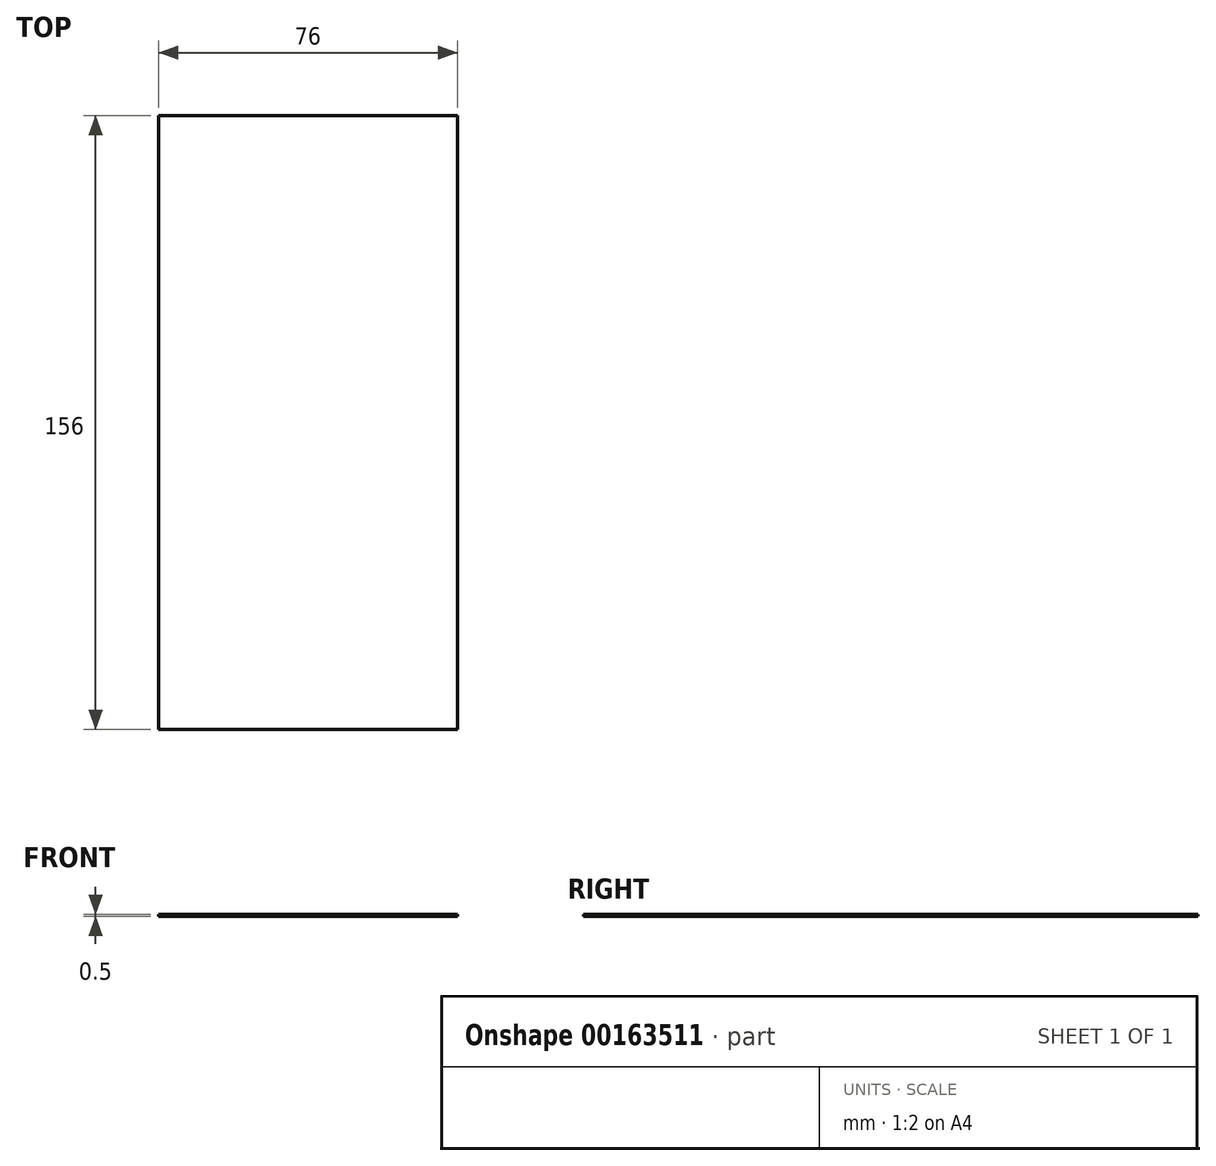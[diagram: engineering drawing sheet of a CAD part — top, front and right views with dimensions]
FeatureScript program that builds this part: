
annotation { "Feature Type Name" : "Feature", "Feature Type Description" : "" }
export const myFeature = defineFeature(function(context is Context, id is Id, definition is map)
    precondition{}
    {
        {
            var Q0;
            Q0=qCreatedBy(makeId("Top.planeOp"),FACE);
            var sketch = newSketch(context, id + "F0", { "sketchPlane" : qUnion([Q0])});
            skLineSegment(sketch, "E0.bottom", {"start": v(-61.13, 60.83) * mm, "end": v(14.87, 60.83) * mm});
            skLineSegment(sketch, "E0.top", {"start": v(-61.13, -95.17) * mm, "end": v(14.87, -95.17) * mm});
            skLineSegment(sketch, "E0.left", {"start": v(-61.13, 60.83) * mm, "end": v(-61.13, -95.17) * mm});
            skLineSegment(sketch, "E0.right", {"start": v(14.87, 60.83) * mm, "end": v(14.87, -95.17) * mm});
            skSolve(sketch);
        }
        {
            var Q0;
            Q0=makeQuery(id+"F0.imprint","IMPRINT",FACE,{"disambiguationData":[TD([[makeQuery(id+"F0.imprint","IMPRINT",EDGE,{"derivedFrom":sQuery(id+"F0.wireOp",EDGE,"E0.bottom")}),-1.0]])]});
            extrude(context, id + "F1", {"entities" : qUnion([Q0]), "depth" : 0.5 * mm});
        }
    });
